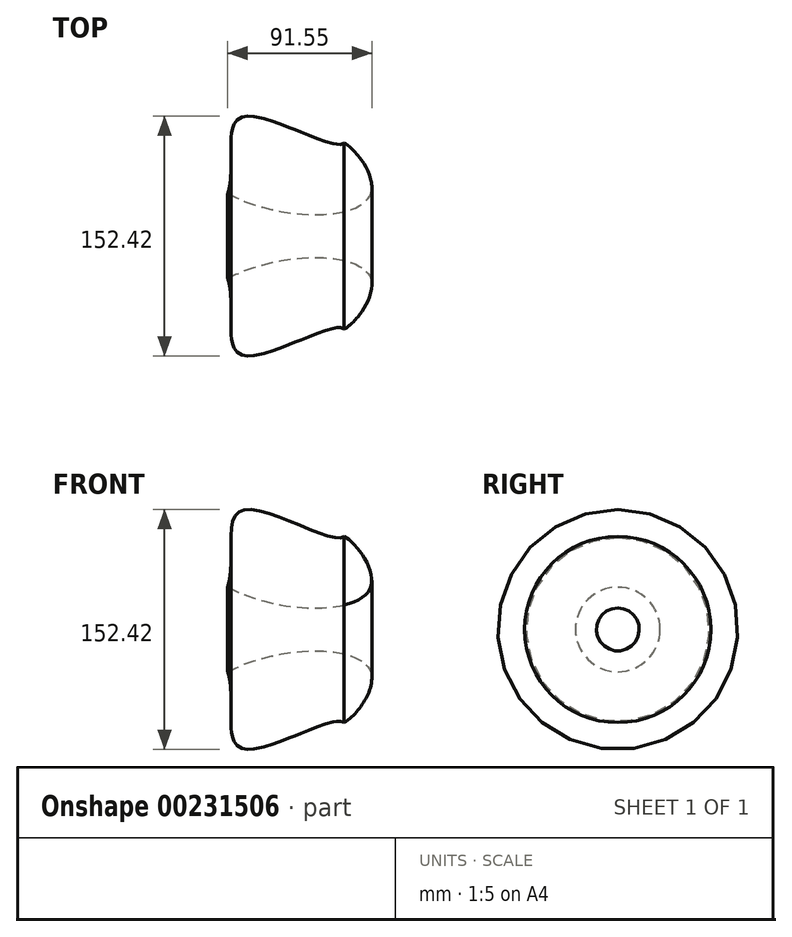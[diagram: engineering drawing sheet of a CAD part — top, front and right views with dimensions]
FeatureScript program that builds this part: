
annotation { "Feature Type Name" : "Feature", "Feature Type Description" : "" }
export const myFeature = defineFeature(function(context is Context, id is Id, definition is map)
    precondition{}
    {
        {
            var Q0;
            Q0=qCreatedBy(makeId("Front.planeOp"),FACE);
            var sketch = newSketch(context, id + "F0", { "sketchPlane" : qUnion([Q0])});
            skFitSpline(sketch, "E0", {"points": [v(0, 26.86) * mm, v(9.14, 75.66) * mm, v(74, 59.17) * mm], "startDerivative": vector(36.62, 106.86) * mm, "endDerivative": vector(37.4, 36.34) * mm});
            skFitSpline(sketch, "E1", {"points": [v(0, 26.86) * mm, v(90.84, 26.86) * mm, v(74, 59.17) * mm], "startDerivative": vector(169.85, -88.28) * mm, "endDerivative": vector(-55.96, 28.8) * mm});
            skLineSegment(sketch, "E2", {"start": v(0, 0) * mm, "end": v(70.39, 0) * mm, "construction": true});
            skLineSegment(sketch, "E3", {"start": v(0, 0) * mm, "end": v(0, 37.88) * mm, "construction": true});
            skSolve(sketch);
        }
        {
            var Q0;
            Q0=makeQuery(id+"F0.imprint","IMPRINT",FACE,{"disambiguationData":[TD([[makeQuery(id+"F0.imprint","IMPRINT",EDGE,{"derivedFrom":sQuery(id+"F0.wireOp",EDGE,"E0")}),-1.0]])]});
            var Q1;
            Q1=sQuery(id+"F0.wireOp",EDGE,"E2");
            revolve(context, id + "F1", {"surfaceOperationType" : NewSurfaceOperationType.NEW, "entities" : qUnion([Q0]), "axis" : qUnion([Q1]), "revolveType" : RevolveType.FULL});
        }
    });
